# Revit family: Kitchen_Taps-Mixers_hansgrohe_76837XXX-Aqittura-M91-SodaSystem-240-1je_
name_source: partatom
category: Plumbing Fixtures
revit_build: Autodesk Revit 2018 (Build: 20170223_1515(x64)
units: mm (PartAtom-declared; Revit-internal decimal feet)

## family parameters
Always vertical = No
Cut with Voids When Loaded = No
OmniClass Number = 23.31.11.15.11
OmniClass Title = Sink Cartridge Faucets
Part Type = Normal
Room Calculation Point = No
Round Connector Dimension = Use Diameter
Shared = No
Work Plane-Based = Yes

## types (3) — shared parameters
Always visible = Yes
BIMobject category = Taps & Mixers
Cold Water Inlet = 10 mm
Cold Water Inlet Description = Cold Water Inlet 9.5mm
Default Elevation = 1219.2 mm  [stored 4 ft]
Description = Aqittura M91 SodaSystem 240, 1jet
Design country = Germany
EAN code = 4059625409824
Edition number = 1
GTIN code = https://4059625409824
Hot Water Inlet = 10 mm
Hot Water Inlet Description = Hot Water Inlet 9.5mm
IFC Classification = Valve
Manufacturer = Hansgrohe
Manufacturer country = Germany
Manufacturer name = hansgrohe
Model = 76837XXX
OmniClass Code = 23-31 11 15 11
OmniClass Description = Sink Cartridge Faucets
Product Guid = e59b4beb-2295-4c06-af42-97dc63301e5a
Product SKU = 76837XXX
Product data url = https://bimobject.com
Product family = Aqittura M91
Product group = Kitchen mixers
Product name = 76837XXX Aqittura M91 SodaSystem 240, 1jet
QR code = https://bimobject.com
URL = https://www.hansgrohe.com
Weight Net (Kg) = 26.6

## per-type parameters (varying)
| type | Material 1 |
| 670 Matt Black | Hansgrohe - Metal - 670 Matt Black |
| 800 Stainless Steel Optic | Hansgrohe - Metal - 800 Stainless Steel Optic |
| 000 Chrome | Hansgrohe - Metal - 000 Chrome |

note: [stored X ft] marks values corroborated as IEEE doubles in the binary element streams (Revit-internal decimal feet)

## geometry (parser evidence)
native form markers: Sweep x1
no freeform markers — native parametric forms only
